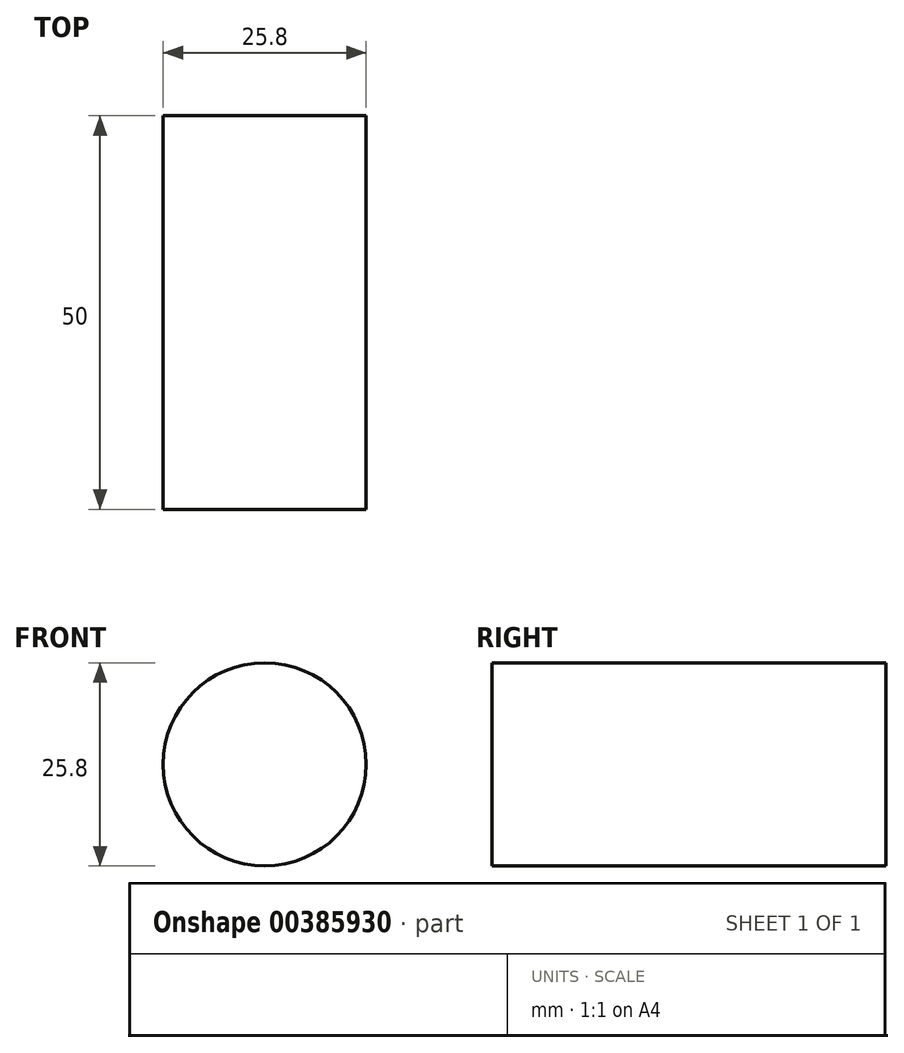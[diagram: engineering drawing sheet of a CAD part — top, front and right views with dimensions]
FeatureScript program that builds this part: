
annotation { "Feature Type Name" : "Feature", "Feature Type Description" : "" }
export const myFeature = defineFeature(function(context is Context, id is Id, definition is map)
    precondition{}
    {
        {
            var Q0;
            Q0=qCreatedBy(makeId("Front.planeOp"),FACE);
            var sketch = newSketch(context, id + "F0", { "sketchPlane" : qUnion([Q0])});
            skCircle(sketch, "E0", {"center": v(0, 0) * mm, "radius": 12.9 * mm});
            skSolve(sketch);
        }
        {
            var Q0;
            Q0 = qSketchRegion(id + "F0", true);
            extrude(context, id + "F1", {"entities" : qUnion([Q0]), "depth" : 50 * mm});
        }
    });
